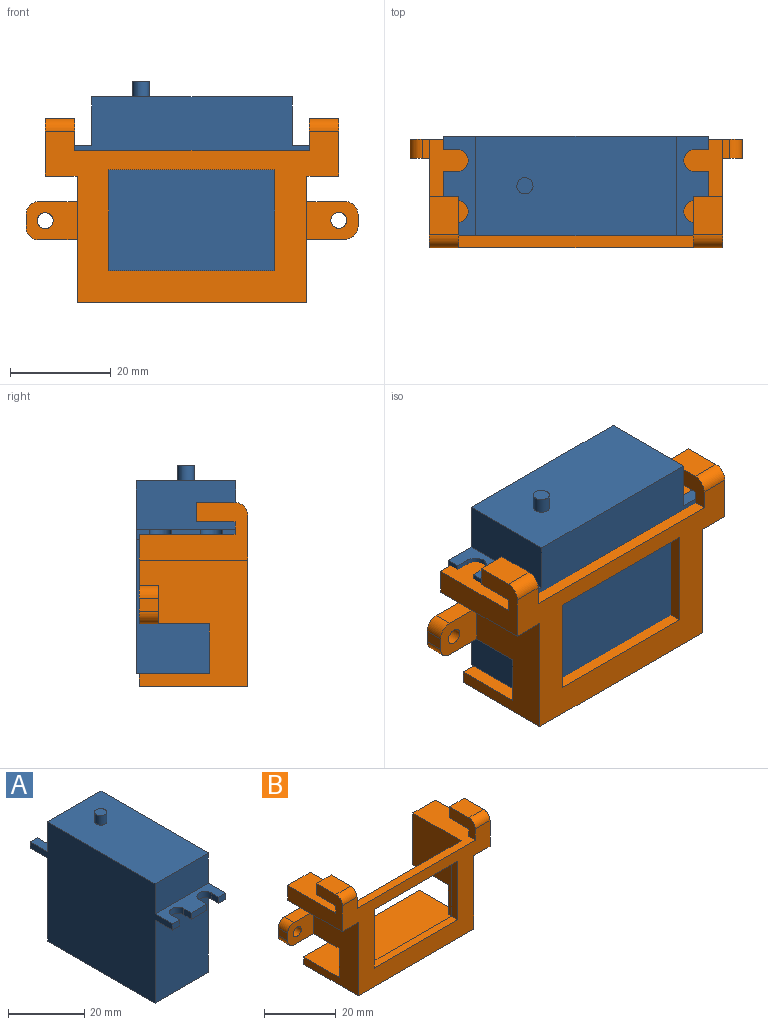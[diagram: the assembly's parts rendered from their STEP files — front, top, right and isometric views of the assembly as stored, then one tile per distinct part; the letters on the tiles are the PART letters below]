
ASSEMBLY  parts=2 mates=1
PART A: 32 faces, bbox 19.8x52.8x41.4 mm
  f0: plane 26.67x19.82mm, normal (0,-1,0), area 528.6mm2, adj f4,f6,f9,f31
  f1: plane 26.67x19.82mm, normal (0,1,0), area 528.6mm2, adj f4,f6,f9,f20
  f2: cylinder r=1.61mm len=3.22mm, axis (0,0,-1), area 30.9mm2, adj f3,f8
  f3: plane 3.22x3.22mm, normal (0,0,1), area 8.1mm2, adj f2
  f4: plane 52.84x38.35mm, normal (-1,0,0), area 1555.3mm2, adj f0,f1,f5,f7,f8,f9,f10,f19
  f5: plane 19.82x9.68mm, normal (0,-1,0), area 191.9mm2, adj f4,f6,f8,f30
  f6: plane 52.84x38.35mm, normal (1,0,0), area 1555.3mm2, adj f0,f1,f5,f7,f8,f9,f11,f19
  f7: plane 19.82x9.68mm, normal (0,1,0), area 191.9mm2, adj f4,f6,f8,f19
  f8: plane 39.88x19.82mm, normal (0,0,1), area 782.3mm2, adj f2,f4,f5,f6,f7
  f9: plane 39.88x19.82mm, normal (0,0,-1), area 790.4mm2, adj f0,f1,f4,f6
  f10: plane 2.64x2mm, normal (0,1,0), area 5.3mm2, adj f4,f18,f19,f20
  f11: plane 2.64x2mm, normal (0,1,0), area 5.3mm2, adj f6,f12,f19,f20
  f12: plane 2.79x2mm, normal (-1,0,0), area 5.6mm2, adj f11,f13,f19,f20
  f13: cylinder r=2.19mm len=4.38mm, axis (0,0,-1), area 13.8mm2, adj f12,f14,f19,f20
  f14: plane 2.79x2mm, normal (1,0,0), area 5.6mm2, adj f13,f15,f19,f20
  f15: plane 5.79x2mm, normal (0,1,0), area 11.6mm2, adj f14,f16,f19,f20
  f16: plane 2.79x2mm, normal (-1,0,0), area 5.6mm2, adj f15,f17,f19,f20
  f17: cylinder r=2.19mm len=4.38mm, axis (0,0,-1), area 13.8mm2, adj f16,f18,f19,f20
  f18: plane 2.79x2mm, normal (1,0,0), area 5.6mm2, adj f10,f17,f19,f20
  f19: plane 19.82x6.48mm, normal (0,0,1), area 88.9mm2, adj f4,f6,f7,f10,f11,f12,f13,f14
  f20: plane 19.82x6.48mm, normal (0,0,-1), area 88.9mm2, adj f1,f4,f6,f10,f11,f12,f13,f14
  f21: plane 2.64x2mm, normal (0,-1,0), area 5.3mm2, adj f4,f22,f30,f31
  f22: plane 2.79x2mm, normal (1,0,0), area 5.6mm2, adj f21,f23,f30,f31
  f23: cylinder r=2.19mm len=4.38mm, axis (0,0,-1), area 13.8mm2, adj f22,f24,f30,f31
  f24: plane 2.79x2mm, normal (-1,0,0), area 5.6mm2, adj f23,f25,f30,f31
  f25: plane 5.79x2mm, normal (0,-1,0), area 11.6mm2, adj f24,f26,f30,f31
  f26: plane 2.79x2mm, normal (1,0,0), area 5.6mm2, adj f25,f27,f30,f31
  f27: cylinder r=2.19mm len=4.38mm, axis (0,0,-1), area 13.8mm2, adj f26,f28,f30,f31
  f28: plane 2.79x2mm, normal (-1,0,0), area 5.6mm2, adj f27,f29,f30,f31
  f29: plane 2.64x2mm, normal (0,-1,0), area 5.3mm2, adj f6,f28,f30,f31
  f30: plane 19.82x6.48mm, normal (0,0,1), area 88.9mm2, adj f4,f5,f6,f21,f22,f23,f24,f25
  f31: plane 19.82x6.48mm, normal (0,0,-1), area 88.9mm2, adj f0,f4,f6,f21,f22,f23,f24,f25
PART B: 48 faces, bbox 66x21.6x36.6 mm
  f0: plane 45.72x2.54mm, normal (0,1,0), area 116.1mm2, adj f3,f5,f8,f9
  f1: plane 17.78x12.7mm, normal (0,1,0), area 144.2mm2, adj f2,f9,f10,f11,f12,f19,f20,f21
  f2: plane 27.69x19.05mm, normal (1,0,0), area 389mm2, adj f1,f3,f12,f21,f23,f29
  f3: plane 45.72x19.05mm, normal (0,0,1), area 845.2mm2, adj f0,f2,f4,f8,f9,f23,f28,f29
  f4: plane 27.69x19.05mm, normal (-1,0,0), area 387.3mm2, adj f3,f12,f13,f15,f23,f28
  f5: plane 45.72x21.59mm, normal (0,0,-1), area 987.1mm2, adj f0,f8,f9,f14
  f6: plane 21.59x11.43mm, normal (1,0,0), area 153.5mm2, adj f7,f12,f13,f14,f32,f33,f34,f35
  f7: plane 21.59x6.35mm, normal (0,0,-1), area 137.1mm2, adj f6,f8,f13,f14
  f8: plane 25.15x21.59mm, normal (1,0,0), area 374.2mm2, adj f0,f3,f5,f7,f13,f14,f15,f17
  f9: plane 25.15x21.59mm, normal (-1,0,0), area 375.5mm2, adj f0,f1,f3,f5,f10,f14,f19,f21
  f10: plane 21.59x6.35mm, normal (0,0,-1), area 137.1mm2, adj f1,f9,f11,f14
  f11: plane 21.59x11.43mm, normal (-1,0,0), area 153.5mm2, adj f1,f10,f12,f14,f37,f38,f39,f40
  f12: plane 58.42x21.59mm, normal (0,0,1), area 457.4mm2, adj f1,f2,f4,f6,f11,f13,f14,f23
  f13: plane 17.65x12.7mm, normal (0,1,0), area 142.5mm2, adj f4,f6,f7,f8,f12,f15,f16,f17
  f14: plane 58.42x34.04mm, normal (0,-1,0), area 828.4mm2, adj f5,f6,f7,f8,f9,f10,f11,f12
  f15: plane 13.97x10.16mm, normal (0,0,-1), area 64.5mm2, adj f4,f8,f13,f18,f28,f47
  f16: plane 3.81x2.41mm, normal (1,0,0), area 9.2mm2, adj f13,f18,f46,f47
  f17: plane 7.62x3.81mm, normal (0,0,1), area 29mm2, adj f8,f13,f18,f46
  f18: plane 10.16x7.49mm, normal (0,-1,0), area 65.4mm2, adj f8,f15,f16,f17,f30,f46,f47
  f19: plane 7.62x3.81mm, normal (0,0,1), area 29mm2, adj f1,f9,f22,f44
  f20: plane 3.81x2.54mm, normal (-1,0,0), area 9.7mm2, adj f1,f22,f44,f45
  f21: plane 13.97x10.16mm, normal (0,0,-1), area 64.5mm2, adj f1,f2,f9,f22,f29,f45
  f22: plane 10.16x7.62mm, normal (0,-1,0), area 66.7mm2, adj f9,f19,f20,f21,f31,f44,f45
  f23: plane 40.64x27.69mm, normal (0,1,0), area 462.6mm2, adj f2,f3,f4,f12,f24,f25,f26,f27
  f24: plane 33.02x2.54mm, normal (0,0,1), area 83.9mm2, adj f14,f23,f25,f27
  f25: plane 20.07x2.54mm, normal (1,0,0), area 51mm2, adj f14,f23,f24,f26
  f26: plane 33.02x2.54mm, normal (0,0,-1), area 83.9mm2, adj f14,f23,f25,f27
  f27: plane 20.07x2.54mm, normal (-1,0,0), area 51mm2, adj f14,f23,f24,f26
  f28: plane 10.03x2.54mm, normal (0,1,0), area 25.5mm2, adj f3,f4,f8,f15
  f29: plane 9.91x2.54mm, normal (0,1,0), area 25.2mm2, adj f2,f3,f9,f21
  f30: cylinder r=1.59mm len=3.81mm, axis (0,-1,0), area 38mm2, adj f13,f18
  f31: cylinder r=1.59mm len=3.81mm, axis (0,-1,0), area 38mm2, adj f1,f22
  f32: plane 7.62x5.84mm, normal (0,0,1), area 44.5mm2, adj f6,f33,f36,f42
  f33: plane 5.84x3.81mm, normal (0,1,0), area 22.3mm2, adj f6,f32,f34,f36
  f34: plane 7.62x5.84mm, normal (0,0,-1), area 44.5mm2, adj f6,f33,f35,f36
  f35: plane 5.84x2.54mm, normal (0,1,0), area 14.8mm2, adj f6,f12,f34,f36
  f36: plane 10.16x6.35mm, normal (-1,0,0), area 43.8mm2, adj f12,f14,f32,f33,f34,f35,f42
  f37: plane 5.84x2.54mm, normal (0,1,0), area 14.8mm2, adj f11,f12,f38,f41
  f38: plane 7.62x5.84mm, normal (0,0,-1), area 44.5mm2, adj f11,f37,f39,f41
  f39: plane 5.84x3.81mm, normal (0,1,0), area 22.3mm2, adj f11,f38,f40,f41
  f40: plane 7.62x5.84mm, normal (0,0,1), area 44.5mm2, adj f11,f39,f41,f43
  f41: plane 10.16x6.35mm, normal (1,0,0), area 43.8mm2, adj f12,f14,f37,f38,f39,f40,f43
  f42: cylinder r=2.54mm len=5.84mm, axis (1,0,0), area 23.3mm2, adj f6,f14,f32,f36
  f43: cylinder r=2.54mm len=5.84mm, axis (1,0,0), area 23.3mm2, adj f11,f14,f40,f41
  f44: cylinder r=2.54mm len=3.81mm, axis (0,1,0), area 15.2mm2, adj f1,f19,f20,f22
  f45: cylinder r=2.54mm len=3.81mm, axis (0,1,0), area 15.2mm2, adj f1,f20,f21,f22
  f46: cylinder r=2.54mm len=3.81mm, axis (0,1,0), area 15.2mm2, adj f13,f16,f17,f18
  f47: cylinder r=2.54mm len=3.81mm, axis (0,1,0), area 15.2mm2, adj f13,f15,f16,f18
PLACE A rot(axis=(0,0,1),90deg) t=(-1.98,-6.86,-21.46)mm
PLACE B t=(-1.98,-19.13,6.22)mm
MATE fastened A.f9 <-> B.f3  axis (0,0,-1) through (-1.98,-6.86,-21.46)mm
